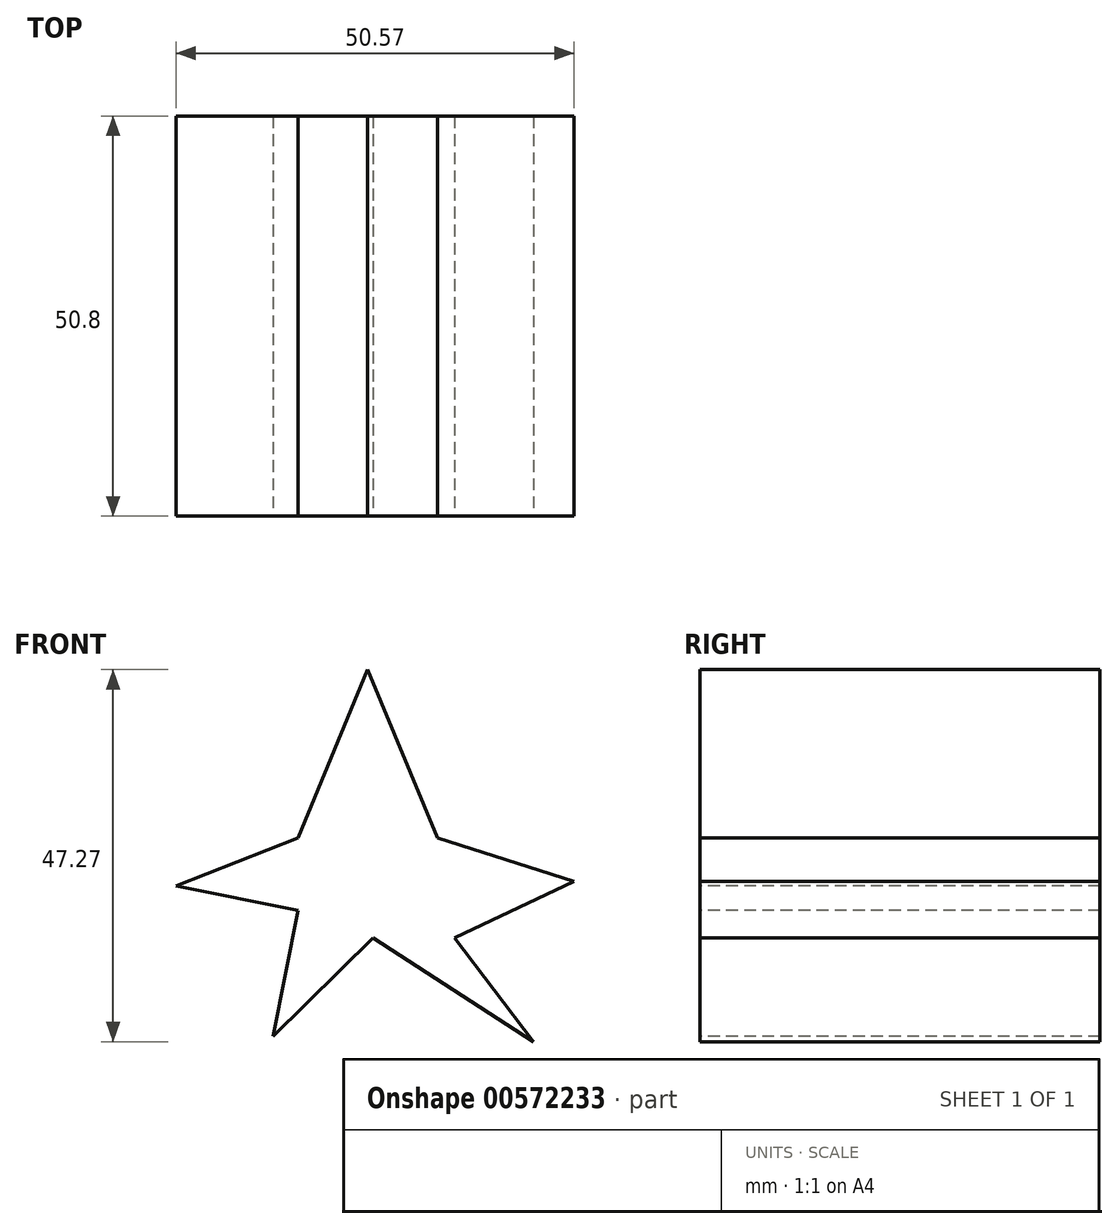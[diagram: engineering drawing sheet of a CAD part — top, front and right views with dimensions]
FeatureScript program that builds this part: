
annotation { "Feature Type Name" : "Feature", "Feature Type Description" : "" }
export const myFeature = defineFeature(function(context is Context, id is Id, definition is map)
    precondition{}
    {
        {
            var Q0;
            Q0=qCreatedBy(makeId("Front.planeOp"),FACE);
            var sketch = newSketch(context, id + "F0", { "sketchPlane" : qUnion([Q0])});
            skLineSegment(sketch, "E0", {"start": v(0, 0) * mm, "end": v(8.85, 21.38) * mm});
            skLineSegment(sketch, "E1", {"start": v(8.85, 21.38) * mm, "end": v(17.7, 0) * mm});
            skLineSegment(sketch, "E2", {"start": v(17.7, 0) * mm, "end": v(35.08, -5.51) * mm});
            skLineSegment(sketch, "E3", {"start": v(35.08, -5.51) * mm, "end": v(19.88, -12.7) * mm});
            skLineSegment(sketch, "E4", {"start": v(19.88, -12.7) * mm, "end": v(29.9, -25.9) * mm});
            skLineSegment(sketch, "E5", {"start": v(29.9, -25.9) * mm, "end": v(9.52, -12.7) * mm});
            skLineSegment(sketch, "E6", {"start": v(9.52, -12.7) * mm, "end": v(-3.17, -25.22) * mm});
            skLineSegment(sketch, "E7", {"start": v(-3.17, -25.22) * mm, "end": v(0, -9.19) * mm});
            skLineSegment(sketch, "E8", {"start": v(0, -9.19) * mm, "end": v(-15.49, -6.12) * mm});
            skLineSegment(sketch, "E9", {"start": v(0, 0) * mm, "end": v(-15.49, -6.12) * mm});
            skSolve(sketch);
        }
        {
            var Q0;
            Q0=makeQuery(id+"F0.imprint","IMPRINT",FACE,{"disambiguationData":[TD([[makeQuery(id+"F0.imprint","IMPRINT",EDGE,{"derivedFrom":sQuery(id+"F0.wireOp",EDGE,"E0")}),-1.0]])]});
            extrude(context, id + "F1", {"entities" : qUnion([Q0]), "oppositeDirection" : true, "depth" : 50.8 * mm, "offsetDistance" : 25.4 * mm});
        }
    });
